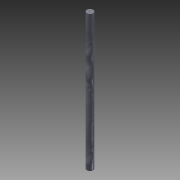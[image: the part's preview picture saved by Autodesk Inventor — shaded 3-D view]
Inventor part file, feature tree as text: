
AUTODESK INVENTOR PART (.ipt)
format: ipt  version: 2015 (Build 190159000, 159)  size: 86,528 bytes
history: native  units: mm
features: other x1, extrude x1, sketch x1
ambient origin geometry x8: Origin, YZ Plane, XZ Plane, XY Plane, X Axis, Y Axis, Z Axis, Center Point
bodies: Body1 (feature_tree)
feature tree (3):
  other  "ソリッド1"
  extrude  "押し出し1"  Depth=3.0mm
  sketch  "スケッチ1"
